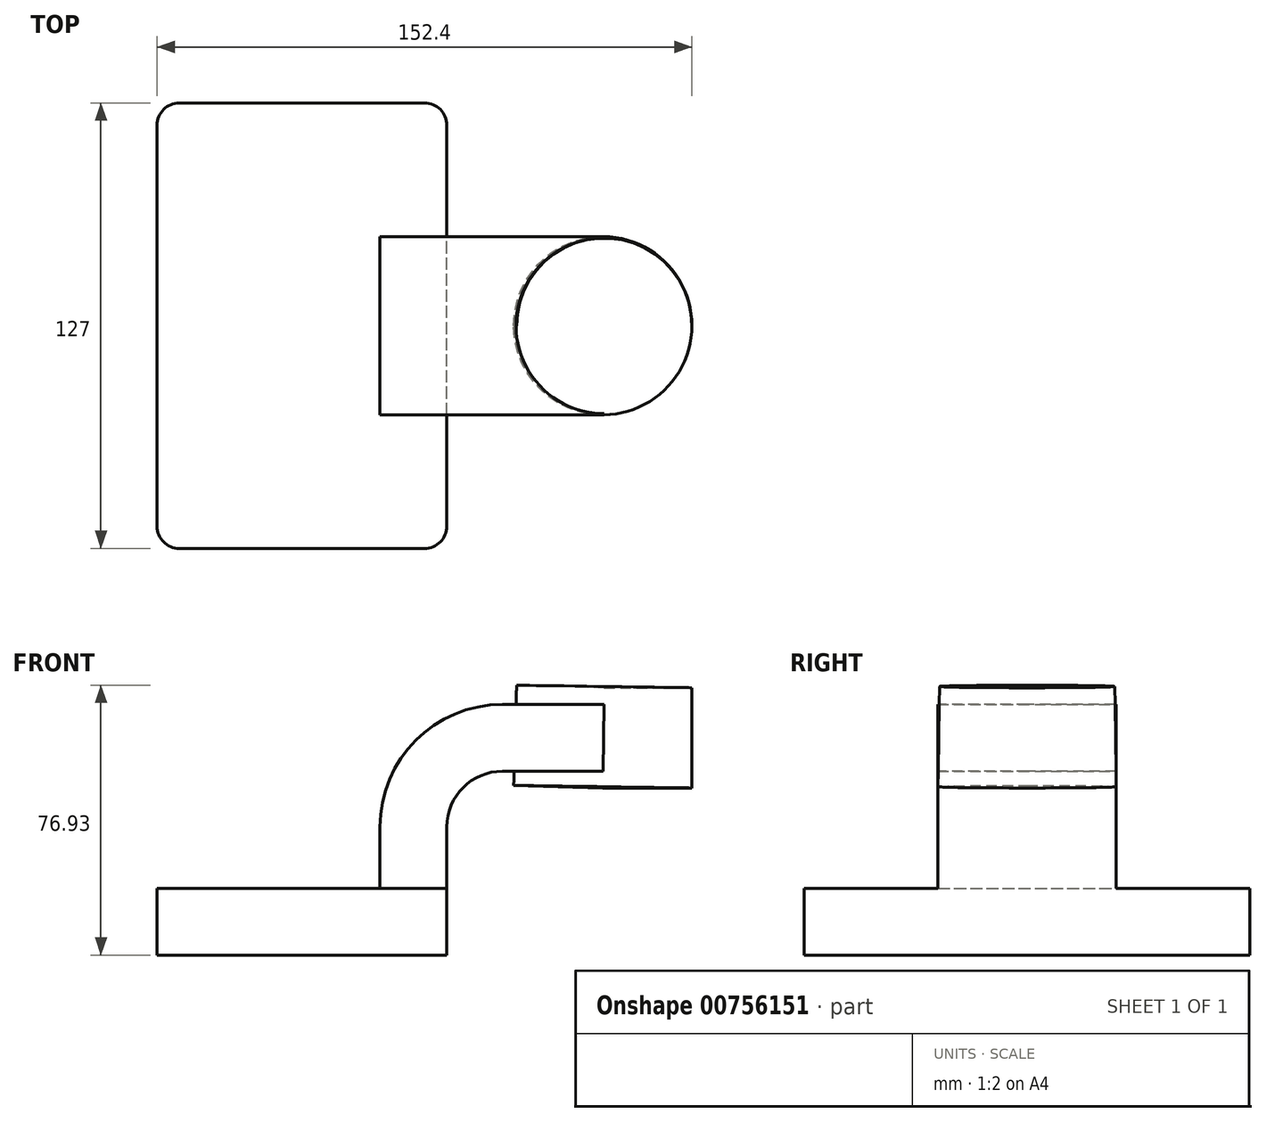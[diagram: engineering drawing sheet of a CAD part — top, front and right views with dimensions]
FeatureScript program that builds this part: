
annotation { "Feature Type Name" : "Feature", "Feature Type Description" : "" }
export const myFeature = defineFeature(function(context is Context, id is Id, definition is map)
    precondition{}
    {
        {
            var Q0;
            Q0=qCreatedBy(makeId("Front.planeOp"),FACE);
            var sketch = newSketch(context, id + "F0", { "sketchPlane" : qUnion([Q0])});
            skLineSegment(sketch, "E0.bottom", {"start": v(41.28, -9.52) * mm, "end": v(-41.28, -9.53) * mm});
            skLineSegment(sketch, "E0.top", {"start": v(41.27, 9.53) * mm, "end": v(-41.28, 9.53) * mm});
            skLineSegment(sketch, "E0.left", {"start": v(41.28, -9.52) * mm, "end": v(41.28, 9.53) * mm});
            skLineSegment(sketch, "E0.right", {"start": v(-41.28, -9.53) * mm, "end": v(-41.28, 9.53) * mm});
            skPoint(sketch, "E0.middle", {"position": v(0, 0) * mm});
            skLineSegment(sketch, "E1.bottom", {"start": v(111.12, 66.68) * mm, "end": v(60.32, 66.68) * mm});
            skLineSegment(sketch, "E1.top", {"start": v(111.12, 38.1) * mm, "end": v(60.32, 38.1) * mm});
            skLineSegment(sketch, "E1.left", {"start": v(111.12, 38.1) * mm, "end": v(111.12, 66.68) * mm});
            skLineSegment(sketch, "E1.right", {"start": v(60.32, 38.1) * mm, "end": v(60.32, 66.68) * mm});
            skPoint(sketch, "E1.middle", {"position": v(85.72, 52.39) * mm});
            skLineSegment(sketch, "E2", {"start": v(41.27, 9.53) * mm, "end": v(41.27, 27) * mm});
            skArc(sketch, "E3", {"start": v(41.28, 27) * mm, "mid": v(45.92, 38.23) * mm, "end": v(57.15, 42.88) * mm});
            skLineSegment(sketch, "E4", {"start": v(57.15, 42.88) * mm, "end": v(86.14, 42.88) * mm});
            skLineSegment(sketch, "E5.0", {"start": v(57.15, 61.93) * mm, "end": v(86.14, 61.93) * mm});
            skArc(sketch, "E5.1", {"start": v(22.23, 27) * mm, "mid": v(32.45, 51.7) * mm, "end": v(57.15, 61.93) * mm});
            skLineSegment(sketch, "E5.2", {"start": v(22.23, 9.53) * mm, "end": v(22.23, 27) * mm});
            skLineSegment(sketch, "E6", {"start": v(85.72, 38.1) * mm, "end": v(86.14, 66.68) * mm});
            skFitSpline(sketch, "E7", {"points": [v(-41.28, 9.53) * mm, v(57.15, 61.93) * mm], "startDerivative": vector(30.41, 107.33) * mm, "endDerivative": vector(177.77, -1.66) * mm});
            skSolve(sketch);
        }
        {
            var Q0;
            Q0=makeQuery(id+"F0.imprint","IMPRINT",FACE,{"disambiguationData":[TD([[makeQuery(id+"F0.imprint","IMPRINT",EDGE,{"derivedFrom":sQuery(id+"F0.wireOp",EDGE,"E0.bottom")}),-1.0]])]});
            extrude(context, id + "F1", {"entities" : qUnion([Q0]), "endBound" : BoundingType.SYMMETRIC, "depth" : 127 * mm, "offsetDistance" : 25.4 * mm});
        }
        {
            var Q0;
            {var subQ0=sQuery(id+"F0.wireOp",EDGE,"E4");var subQ1=sQuery(id+"F0.wireOp",EDGE,"E1.right");var subQ2=makeQuery(id+"F0.imprint","INTERSECT",VERTEX,{"derivedFrom":[subQ1,subQ0]});Q0=makeQuery(id+"F0.imprint","IMPRINT",FACE,{"disambiguationData":[TD([[makeQuery(id+"F0.imprint","IMPRINT",EDGE,{"disambiguationData":[TD([[subQ2,-1.0]])],"derivedFrom":subQ1}),-1.0]])]});}
            var Q1;
            {var subQ1=sQuery(id+"F0.wireOp",EDGE,"E2");Q1=makeQuery(id+"F0.imprint","IMPRINT",FACE,{"disambiguationData":[TD([[makeQuery(id+"F0.imprint","IMPRINT",EDGE,{"derivedFrom":subQ1}),1.0]])]});}
            extrude(context, id + "F2", {"entities" : qUnion([Q0, Q1]), "operationType" : NewBodyOperationType.ADD, "endBound" : BoundingType.SYMMETRIC, "depth" : 50.8 * mm, "offsetDistance" : 25.4 * mm});
        }
        {
            var Q0;
            Q0=makeQuery(id+"F0.imprint","IMPRINT",FACE,{"disambiguationData":[TD([[makeQuery(id+"F0.imprint","IMPRINT",EDGE,{"derivedFrom":sQuery(id+"F0.wireOp",EDGE,"E5.1")}),1.0]])]});
            extrude(context, id + "F3", {"entities" : qUnion([Q0]), "operationType" : NewBodyOperationType.ADD, "endBound" : BoundingType.SYMMETRIC, "depth" : 15.88 * mm, "offsetDistance" : 25.4 * mm});
        }
        {
            var Q0;
            {var subQ4=sQuery(id+"F0.wireOp",EDGE,"E1.left");Q0=makeQuery(id+"F0.imprint","IMPRINT",FACE,{"disambiguationData":[TD([[makeQuery(id+"F0.imprint","IMPRINT",EDGE,{"derivedFrom":subQ4}),1.0]])]});}
            var Q1;
            Q1=sQuery(id+"F0.wireOp",EDGE,"E6");
            revolve(context, id + "F4", {"operationType" : NewBodyOperationType.ADD, "surfaceOperationType" : NewSurfaceOperationType.NEW, "entities" : qUnion([Q0]), "axis" : qUnion([Q1]), "revolveType" : RevolveType.FULL});
        }
        {
            var Q0;
            Q0=makeQuery(id+"F1.opExtrude","CAP_EDGE",EDGE,{"disambiguationData":[OSD([sQuery(id+"F0.wireOp",EDGE,"E0.left")])],"isStart":false});
            var Q1;
            Q1=makeQuery(id+"F1.opExtrude","CAP_EDGE",EDGE,{"disambiguationData":[OSD([sQuery(id+"F0.wireOp",EDGE,"E0.right")])],"isStart":false});
            var Q2;
            Q2=makeQuery(id+"F1.opExtrude","CAP_EDGE",EDGE,{"disambiguationData":[OSD([sQuery(id+"F0.wireOp",EDGE,"E0.right")])],"isStart":true});
            var Q3;
            Q3=makeQuery(id+"F1.opExtrude","CAP_EDGE",EDGE,{"disambiguationData":[OSD([sQuery(id+"F0.wireOp",EDGE,"E0.left")])],"isStart":true});
            fillet(context, id + "F5", {"entities" : qUnion([Q0, Q1, Q2, Q3]), "radius" : 6.35 * mm, "tangentPropagation" : true, "allowEdgeOverflow" : false});
        }
    });
